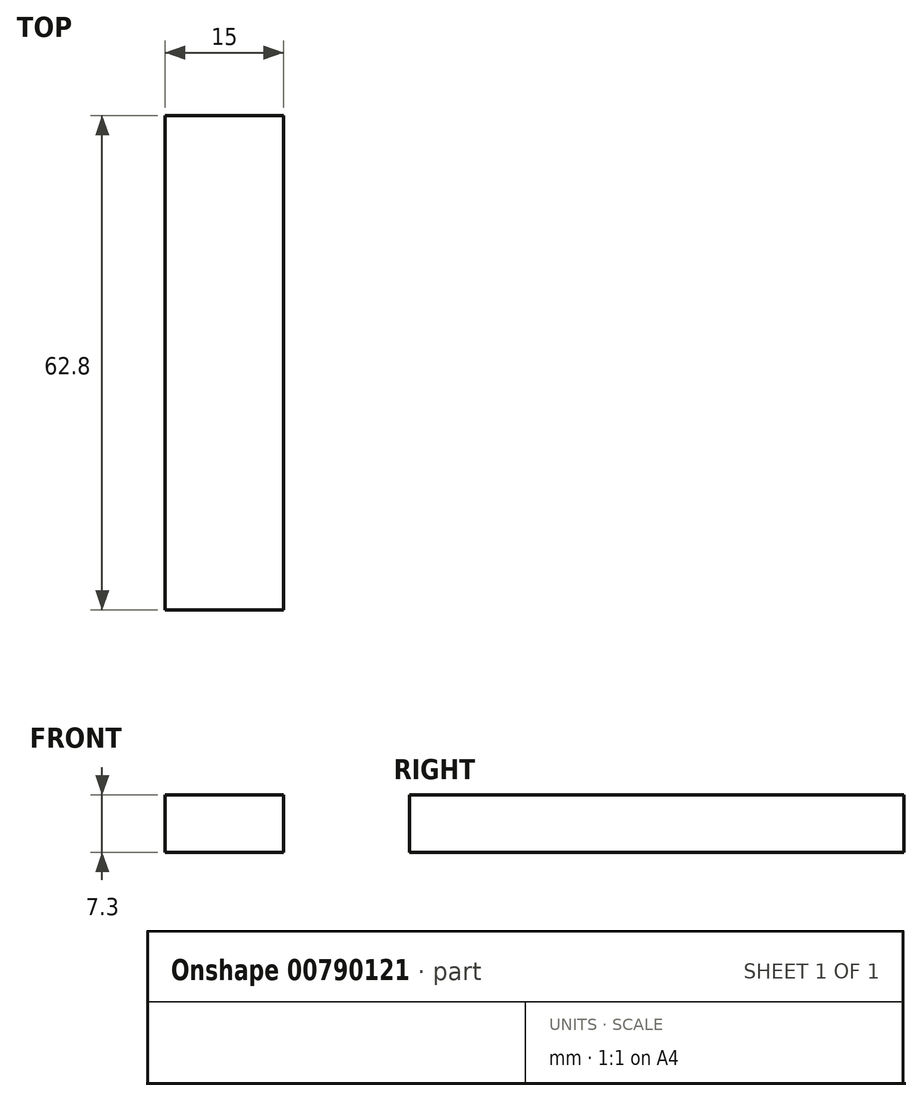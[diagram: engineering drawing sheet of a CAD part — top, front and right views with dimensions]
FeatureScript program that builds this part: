
annotation { "Feature Type Name" : "Feature", "Feature Type Description" : "" }
export const myFeature = defineFeature(function(context is Context, id is Id, definition is map)
    precondition{}
    {
        {
            var Q0;
            Q0=qCreatedBy(makeId("Top.planeOp"),FACE);
            var sketch = newSketch(context, id + "F0", { "sketchPlane" : qUnion([Q0])});
            skLineSegment(sketch, "E0.bottom", {"start": v(-7.5, 31.4) * mm, "end": v(7.5, 31.4) * mm});
            skLineSegment(sketch, "E0.top", {"start": v(-7.5, -31.4) * mm, "end": v(7.5, -31.4) * mm});
            skLineSegment(sketch, "E0.left", {"start": v(-7.5, 31.4) * mm, "end": v(-7.5, -31.4) * mm});
            skLineSegment(sketch, "E0.right", {"start": v(7.5, 31.4) * mm, "end": v(7.5, -31.4) * mm});
            skPoint(sketch, "E0.middle", {"position": v(0, 0) * mm});
            skSolve(sketch);
        }
        {
            var Q0;
            Q0=makeQuery(id+"F0.imprint","IMPRINT",FACE,{"disambiguationData":[TD([[makeQuery(id+"F0.imprint","IMPRINT",EDGE,{"derivedFrom":sQuery(id+"F0.wireOp",EDGE,"E0.bottom")}),-1.0]])]});
            extrude(context, id + "F1", {"entities" : qUnion([Q0]), "depth" : 7.3 * mm});
        }
    });
